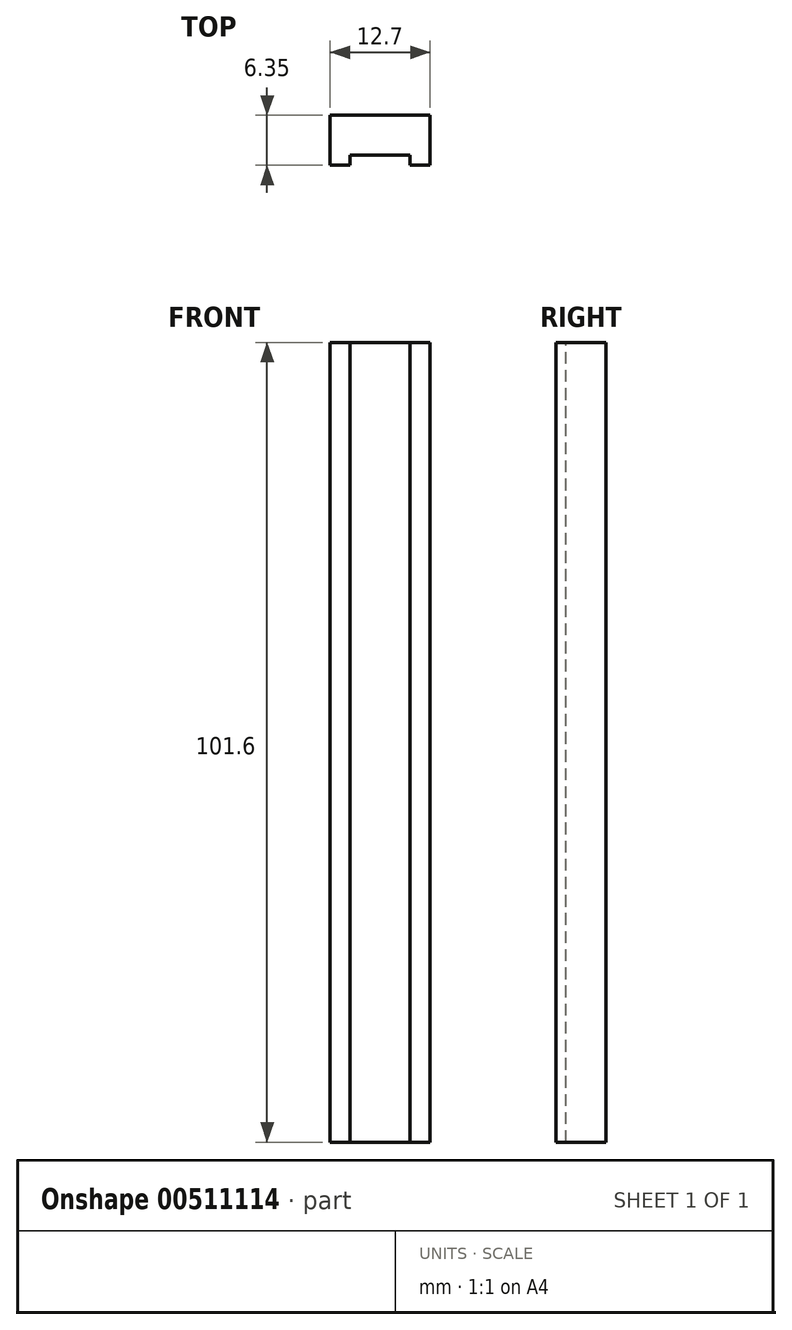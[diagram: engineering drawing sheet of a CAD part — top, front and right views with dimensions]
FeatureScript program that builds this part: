
annotation { "Feature Type Name" : "Feature", "Feature Type Description" : "" }
export const myFeature = defineFeature(function(context is Context, id is Id, definition is map)
    precondition{}
    {
        {
            var Q0;
            Q0=qCreatedBy(makeId("Top.planeOp"),FACE);
            var sketch = newSketch(context, id + "F0", { "sketchPlane" : qUnion([Q0])});
            skLineSegment(sketch, "E0.bottom", {"start": v(0, 0) * mm, "end": v(12.7, 0) * mm});
            skLineSegment(sketch, "E0.top", {"start": v(0, -6.35) * mm, "end": v(12.7, -6.35) * mm});
            skLineSegment(sketch, "E0.left", {"start": v(0, 0) * mm, "end": v(0, -6.35) * mm});
            skLineSegment(sketch, "E0.right", {"start": v(12.7, 0) * mm, "end": v(12.7, -6.35) * mm});
            skSolve(sketch);
        }
        {
            var Q0;
            Q0 = qSketchRegion(id + "F0", true);
            extrude(context, id + "F1", {"entities" : qUnion([Q0]), "depth" : 101.6 * mm});
        }
        {
            var Q0;
            Q0=makeQuery(id+"F1.opExtrude","SWEPT_FACE",FACE,{"disambiguationData":[OSD([sQuery(id+"F0.wireOp",EDGE,"E0.top")])]});
            var sketch = newSketch(context, id + "F2", { "sketchPlane" : qUnion([Q0])});
            skLineSegment(sketch, "E1.bottom", {"start": v(2.54, 0) * mm, "end": v(10.16, 0) * mm});
            skLineSegment(sketch, "E1.top", {"start": v(2.54, 101.6) * mm, "end": v(10.16, 101.6) * mm});
            skLineSegment(sketch, "E1.left", {"start": v(2.54, 0) * mm, "end": v(2.54, 101.6) * mm});
            skLineSegment(sketch, "E1.right", {"start": v(10.16, 0) * mm, "end": v(10.16, 101.6) * mm});
            skSolve(sketch);
        }
        {
            var Q0;
            Q0=makeQuery(id+"F2.imprint","IMPRINT",FACE,{"disambiguationData":[TD([[makeQuery(id+"F2.imprint","IMPRINT",EDGE,{"derivedFrom":sQuery(id+"F2.wireOp",EDGE,"E1.bottom")}),1.0]])]});
            extrude(context, id + "F3", {"entities" : qUnion([Q0]), "operationType" : NewBodyOperationType.REMOVE, "oppositeDirection" : true, "depth" : 1.27 * mm});
        }
    });
